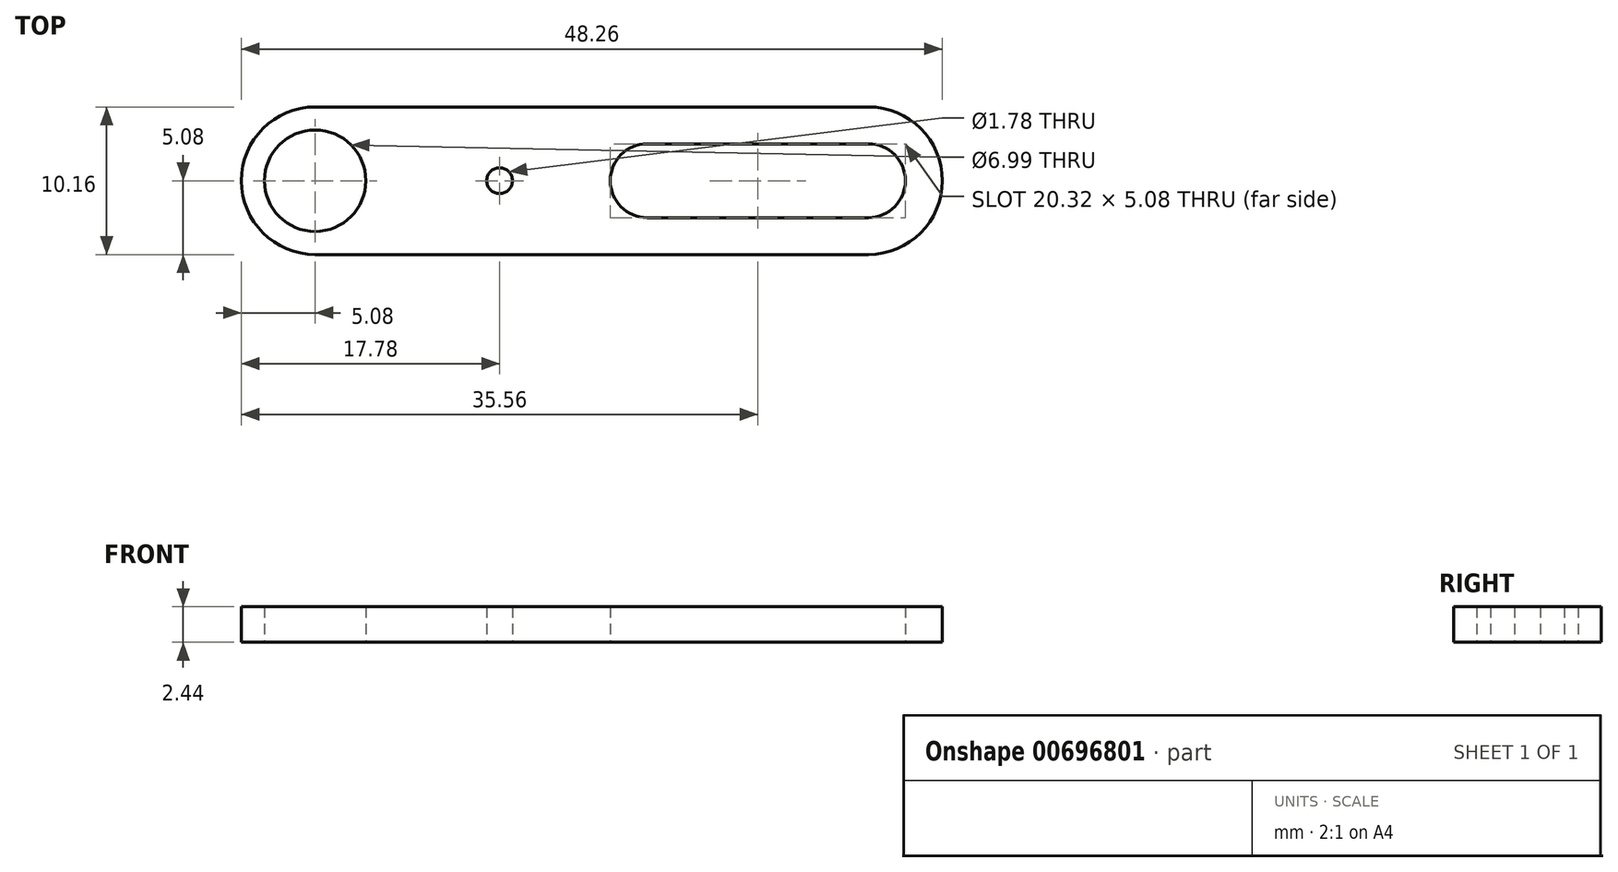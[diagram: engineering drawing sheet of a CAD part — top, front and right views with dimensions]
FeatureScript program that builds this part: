
annotation { "Feature Type Name" : "Feature", "Feature Type Description" : "" }
export const myFeature = defineFeature(function(context is Context, id is Id, definition is map)
    precondition{}
    {
        {
            var Q0;
            Q0=qCreatedBy(makeId("Top.planeOp"),FACE);
            var sketch = newSketch(context, id + "F0", { "sketchPlane" : qUnion([Q0])});
            skArc(sketch, "E0", {"start": v(0, -5.08) * mm, "mid": v(5.08, 0) * mm, "end": v(0, 5.08) * mm});
            skArc(sketch, "E1", {"start": v(-38.1, 5.08) * mm, "mid": v(-43.18, 0) * mm, "end": v(-38.1, -5.08) * mm});
            skLineSegment(sketch, "E2", {"start": v(-38.1, 5.08) * mm, "end": v(0, 5.08) * mm});
            skLineSegment(sketch, "E3", {"start": v(0, -5.08) * mm, "end": v(-38.1, -5.08) * mm});
            skCircle(sketch, "E4", {"center": v(-38.1, 0) * mm, "radius": 3.5 * mm});
            skArc(sketch, "E5", {"start": v(0, -2.54) * mm, "mid": v(2.54, 0) * mm, "end": v(0, 2.54) * mm});
            skArc(sketch, "E6", {"start": v(-15.24, 2.54) * mm, "mid": v(-17.78, 0) * mm, "end": v(-15.24, -2.54) * mm});
            skLineSegment(sketch, "E7", {"start": v(-15.24, 2.54) * mm, "end": v(0, 2.54) * mm});
            skLineSegment(sketch, "E8", {"start": v(0, -2.54) * mm, "end": v(-15.24, -2.54) * mm});
            skCircle(sketch, "E9", {"center": v(-25.4, 0) * mm, "radius": 0.89 * mm});
            skSolve(sketch);
        }
        {
            var Q0;
            Q0=makeQuery(id+"F0.imprint","IMPRINT",FACE,{"disambiguationData":[TD([[makeQuery(id+"F0.imprint","IMPRINT",EDGE,{"derivedFrom":sQuery(id+"F0.wireOp",EDGE,"E0")}),1.0]])]});
            extrude(context, id + "F1", {"entities" : qUnion([Q0]), "depth" : 2.44 * mm, "offsetDistance" : 25.4 * mm});
        }
    });
